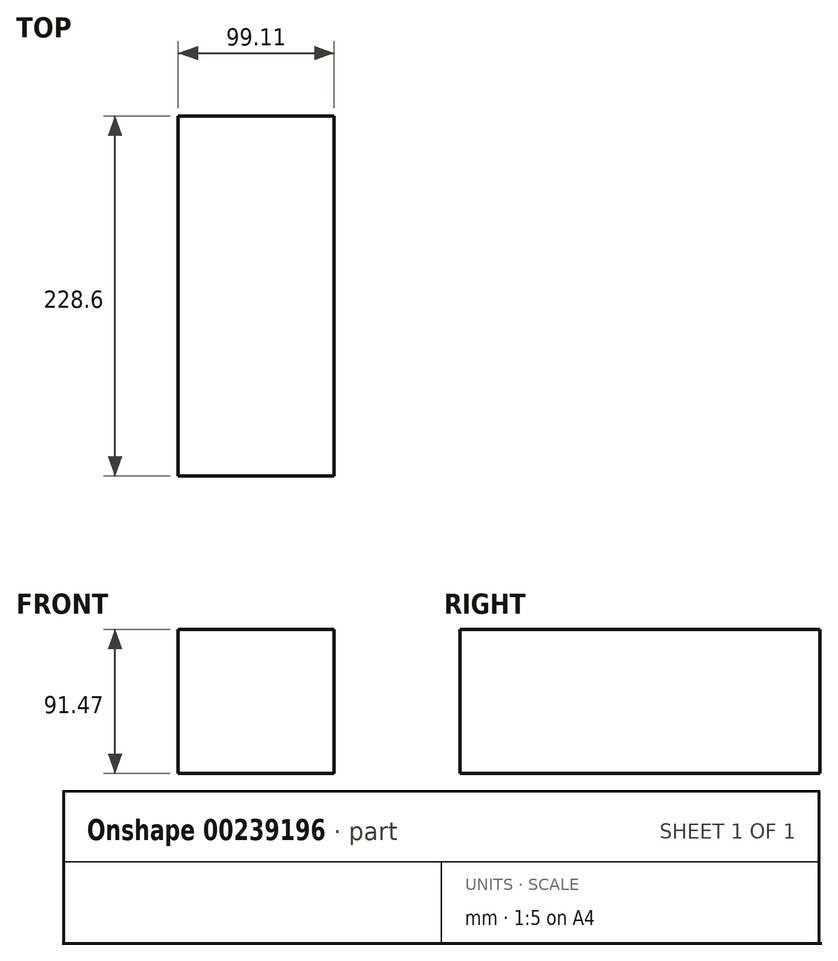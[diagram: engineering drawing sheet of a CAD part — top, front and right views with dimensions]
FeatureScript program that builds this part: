
annotation { "Feature Type Name" : "Feature", "Feature Type Description" : "" }
export const myFeature = defineFeature(function(context is Context, id is Id, definition is map)
    precondition{}
    {
        {
            var Q0;
            Q0=qCreatedBy(makeId("Front.planeOp"),FACE);
            var sketch = newSketch(context, id + "F0", { "sketchPlane" : qUnion([Q0])});
            skLineSegment(sketch, "E0.bottom", {"start": v(-47.4, 44.56) * mm, "end": v(51.7, 44.56) * mm});
            skLineSegment(sketch, "E0.top", {"start": v(-47.4, -46.9) * mm, "end": v(51.7, -46.9) * mm});
            skLineSegment(sketch, "E0.left", {"start": v(-47.4, 44.56) * mm, "end": v(-47.4, -46.9) * mm});
            skLineSegment(sketch, "E0.right", {"start": v(51.7, 44.56) * mm, "end": v(51.7, -46.9) * mm});
            skSolve(sketch);
        }
        {
            var Q0;
            Q0=makeQuery(id+"F0.imprint","IMPRINT",FACE,{"disambiguationData":[TD([[makeQuery(id+"F0.imprint","IMPRINT",EDGE,{"derivedFrom":sQuery(id+"F0.wireOp",EDGE,"E0.bottom")}),-1.0]])]});
            extrude(context, id + "F1", {"entities" : qUnion([Q0]), "depth" : 228.6 * mm});
        }
    });
